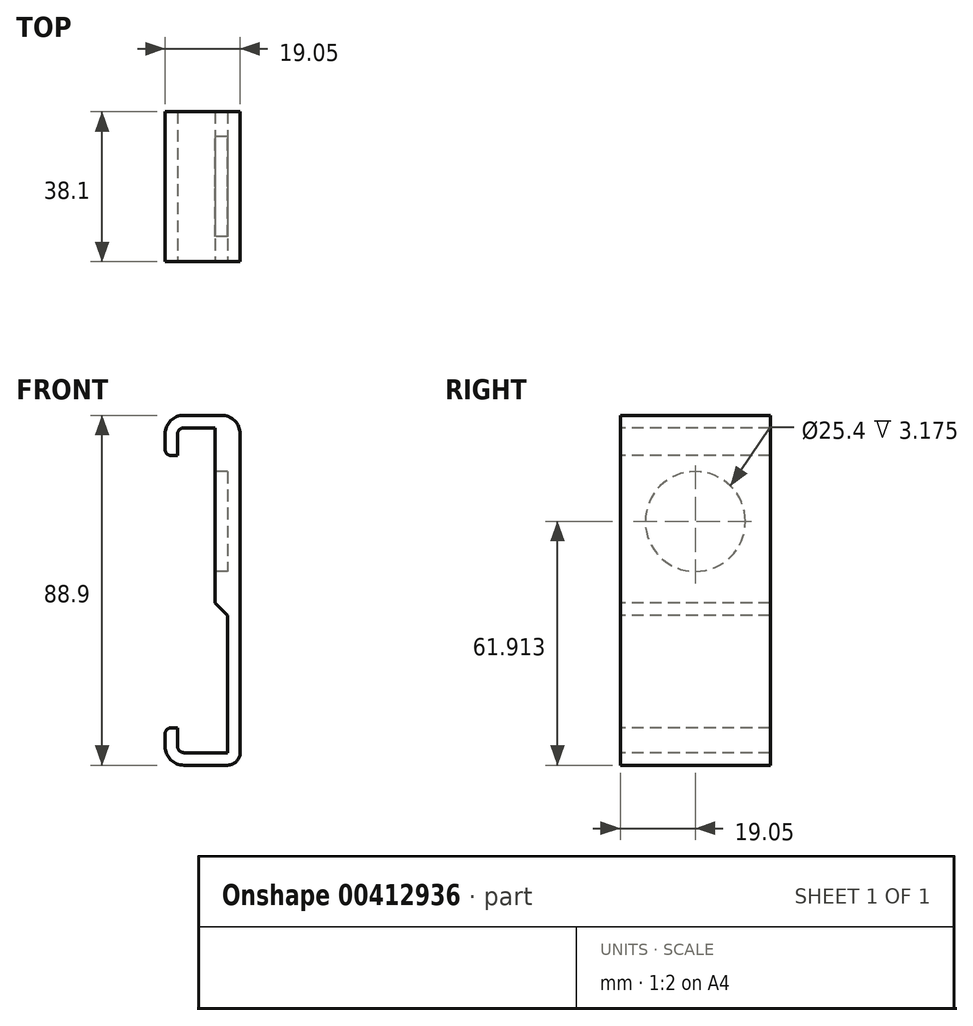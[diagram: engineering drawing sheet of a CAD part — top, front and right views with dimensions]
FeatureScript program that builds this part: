
annotation { "Feature Type Name" : "Feature", "Feature Type Description" : "" }
export const myFeature = defineFeature(function(context is Context, id is Id, definition is map)
    precondition{}
    {
        {
            var Q0;
            Q0=qCreatedBy(makeId("Front.planeOp"),FACE);
            var sketch = newSketch(context, id + "F0", { "sketchPlane" : qUnion([Q0])});
            skLineSegment(sketch, "E0", {"start": v(4.76, 0) * mm, "end": v(15.88, 0) * mm});
            skLineSegment(sketch, "E1", {"start": v(19.05, 3.17) * mm, "end": v(19.05, 84.14) * mm});
            skLineSegment(sketch, "E2", {"start": v(14.29, 88.9) * mm, "end": v(4.76, 88.9) * mm});
            skLineSegment(sketch, "E3", {"start": v(0, 84.14) * mm, "end": v(0, 80.2) * mm});
            skLineSegment(sketch, "E4", {"start": v(0, 4.76) * mm, "end": v(0, 7.94) * mm});
            skLineSegment(sketch, "E5.0", {"start": v(3.18, 84.14) * mm, "end": v(3.18, 78.62) * mm});
            skLineSegment(sketch, "E5.1", {"start": v(3.18, 4.76) * mm, "end": v(3.18, 9.52) * mm});
            skLineSegment(sketch, "E5.2", {"start": v(4.76, 3.17) * mm, "end": v(15.87, 3.17) * mm});
            skLineSegment(sketch, "E5.3", {"start": v(15.87, 3.17) * mm, "end": v(15.87, 38.1) * mm});
            skLineSegment(sketch, "E5.4", {"start": v(12.7, 85.72) * mm, "end": v(4.76, 85.72) * mm});
            skLineSegment(sketch, "E6", {"start": v(1.59, 78.62) * mm, "end": v(1.59, 78.62) * mm});
            skLineSegment(sketch, "E7", {"start": v(1.59, 9.52) * mm, "end": v(3.18, 9.52) * mm});
            skPoint(sketch, "E8.visualSharp", {"position": v(3.18, 3.17) * mm});
            skArc(sketch, "E8.filletArc", {"start": v(3.18, 4.76) * mm, "mid": v(3.64, 3.64) * mm, "end": v(4.76, 3.17) * mm});
            skPoint(sketch, "E9.visualSharp", {"position": v(0, 0) * mm});
            skArc(sketch, "E9.filletArc", {"start": v(0, 4.76) * mm, "mid": v(1.4, 1.4) * mm, "end": v(4.76, 0) * mm});
            skPoint(sketch, "E10.visualSharp", {"position": v(19.05, 0) * mm});
            skArc(sketch, "E10.filletArc", {"start": v(15.88, 0) * mm, "mid": v(18.12, 0.93) * mm, "end": v(19.05, 3.17) * mm});
            skPoint(sketch, "E11.visualSharp", {"position": v(19.05, 88.9) * mm});
            skArc(sketch, "E11.filletArc", {"start": v(19.05, 84.14) * mm, "mid": v(17.66, 87.5) * mm, "end": v(14.29, 88.9) * mm});
            skPoint(sketch, "E12.visualSharp", {"position": v(0, 88.9) * mm});
            skArc(sketch, "E12.filletArc", {"start": v(4.76, 88.9) * mm, "mid": v(1.4, 87.5) * mm, "end": v(0, 84.14) * mm});
            skPoint(sketch, "E13.visualSharp", {"position": v(0, 78.62) * mm});
            skArc(sketch, "E13.filletArc", {"start": v(0, 80.2) * mm, "mid": v(0.46, 79.09) * mm, "end": v(1.59, 78.62) * mm});
            skPoint(sketch, "E14.visualSharp", {"position": v(3.18, 78.62) * mm});
            skPoint(sketch, "E15.visualSharp", {"position": v(3.18, 85.72) * mm});
            skArc(sketch, "E15.filletArc", {"start": v(4.76, 85.72) * mm, "mid": v(3.64, 85.26) * mm, "end": v(3.18, 84.14) * mm});
            skPoint(sketch, "E16.visualSharp", {"position": v(0, 9.52) * mm});
            skArc(sketch, "E16.filletArc", {"start": v(1.59, 9.52) * mm, "mid": v(0.46, 9.06) * mm, "end": v(0, 7.94) * mm});
            skLineSegment(sketch, "E17", {"start": v(1.59, 78.62) * mm, "end": v(3.18, 78.62) * mm});
            skLineSegment(sketch, "E18", {"start": v(15.88, 38.1) * mm, "end": v(12.7, 41.28) * mm});
            skLineSegment(sketch, "E19", {"start": v(12.7, 41.28) * mm, "end": v(12.7, 85.72) * mm});
            skSolve(sketch);
        }
        {
            var Q0;
            Q0=makeQuery(id+"F0.imprint","IMPRINT",FACE,{"disambiguationData":[TD([[makeQuery(id+"F0.imprint","IMPRINT",EDGE,{"derivedFrom":sQuery(id+"F0.wireOp",EDGE,"E0")}),1.0]])]});
            extrude(context, id + "F1", {"entities" : qUnion([Q0]), "oppositeDirection" : true, "depth" : 38.1 * mm});
        }
        {
            var Q0;
            Q0=makeQuery(id+"F1.opExtrude","SWEPT_FACE",FACE,{"disambiguationData":[OSD([sQuery(id+"F0.wireOp",EDGE,"E19")])]});
            var sketch = newSketch(context, id + "F2", { "sketchPlane" : qUnion([Q0])});
            skCircle(sketch, "E20", {"center": v(-19.05, 61.91) * mm, "radius": 12.7 * mm});
            skPoint(sketch, "E20.centerSnap0", {"position": v(-19.05, 41.28) * mm});
            skSolve(sketch);
        }
        {
            var Q0;
            Q0=makeQuery(id+"F2.imprint","IMPRINT",FACE,{"disambiguationData":[TD([[makeQuery(id+"F2.imprint","IMPRINT",EDGE,{"derivedFrom":sQuery(id+"F2.wireOp",EDGE,"E20")}),1.0]])]});
            extrude(context, id + "F3", {"entities" : qUnion([Q0]), "operationType" : NewBodyOperationType.REMOVE, "oppositeDirection" : true, "depth" : 3.17 * mm});
        }
    });
